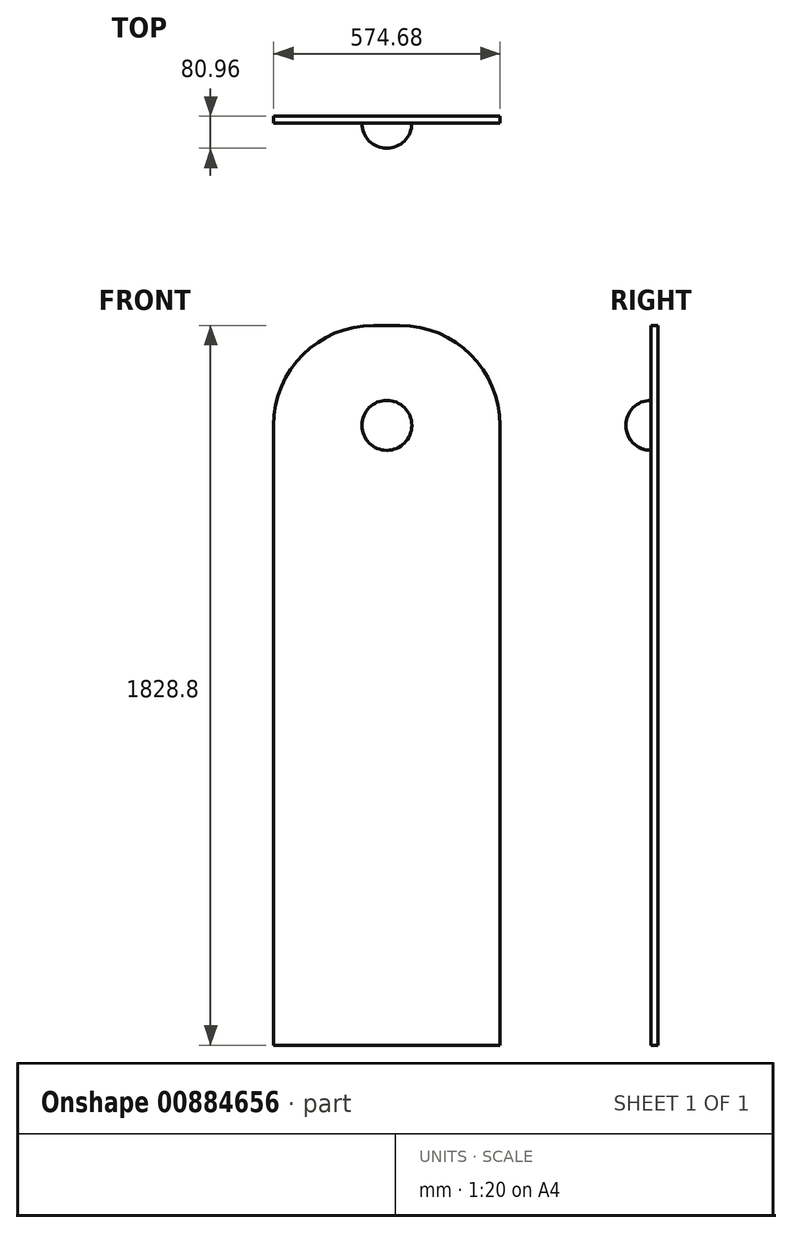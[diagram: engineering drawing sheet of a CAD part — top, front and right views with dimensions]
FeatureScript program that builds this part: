
annotation { "Feature Type Name" : "Feature", "Feature Type Description" : "" }
export const myFeature = defineFeature(function(context is Context, id is Id, definition is map)
    precondition{}
    {
        {
            var Q0;
            Q0=qCreatedBy(makeId("Front.planeOp"),FACE);
            var sketch = newSketch(context, id + "F0", { "sketchPlane" : qUnion([Q0])});
            skLineSegment(sketch, "E0.bottom", {"start": v(-1321.49, 910.36) * mm, "end": v(-746.81, 910.36) * mm});
            skLineSegment(sketch, "E0.top", {"start": v(-1321.49, -918.44) * mm, "end": v(-746.81, -918.44) * mm});
            skLineSegment(sketch, "E0.left", {"start": v(-1321.49, 910.36) * mm, "end": v(-1321.49, -918.44) * mm});
            skLineSegment(sketch, "E0.right", {"start": v(-746.81, 910.36) * mm, "end": v(-746.81, -918.44) * mm});
            skSolve(sketch);
        }
        {
            var Q0;
            Q0=makeQuery(id+"F0.imprint","IMPRINT",FACE,{"disambiguationData":[TD([[makeQuery(id+"F0.imprint","IMPRINT",EDGE,{"derivedFrom":sQuery(id+"F0.wireOp",EDGE,"E0.bottom")}),-1.0]])]});
            extrude(context, id + "F1", {"entities" : qUnion([Q0]), "depth" : 17.46 * mm, "offsetDistance" : 25.4 * mm});
        }
        {
            var Q0;
            Q0=makeQuery(id+"F1.opExtrude","SWEPT_EDGE",EDGE,{"disambiguationData":[OSD([sQuery(id+"F0.wireOp",EDGE,"E0.bottom"),sQuery(id+"F0.wireOp",EDGE,"E0.left")])]});
            fillet(context, id + "F2", {"entities" : qUnion([Q0]), "radius" : 254 * mm, "tangentPropagation" : true, "allowEdgeOverflow" : false});
        }
        {
            var Q0;
            Q0=makeQuery(id+"F1.opExtrude","SWEPT_EDGE",EDGE,{"disambiguationData":[OSD([sQuery(id+"F0.wireOp",EDGE,"E0.bottom"),sQuery(id+"F0.wireOp",EDGE,"E0.right")])]});
            fillet(context, id + "F3", {"entities" : qUnion([Q0]), "radius" : 254 * mm, "tangentPropagation" : true, "allowEdgeOverflow" : false});
        }
        {
            var Q0;
            Q0=makeQuery(id+"F1.opExtrude","CAP_FACE",FACE,{"disambiguationData":[OSD([sQuery(id+"F0.wireOp",EDGE,"E0.bottom"),sQuery(id+"F0.wireOp",EDGE,"E0.top"),sQuery(id+"F0.wireOp",EDGE,"E0.left"),sQuery(id+"F0.wireOp",EDGE,"E0.right")])],"isStart":false});
            var sketch = newSketch(context, id + "F4", { "sketchPlane" : qUnion([Q0])});
            skCircle(sketch, "E1", {"center": v(-1034.15, 656.36) * mm, "radius": 63.5 * mm});
            skSolve(sketch);
        }
        {
            var Q0;
            Q0=makeQuery(id+"F4.imprint","IMPRINT",FACE,{"disambiguationData":[TD([[makeQuery(id+"F4.imprint","IMPRINT",EDGE,{"derivedFrom":sQuery(id+"F4.wireOp",EDGE,"E1")}),1.0]])]});
            extrude(context, id + "F5", {"entities" : qUnion([Q0]), "operationType" : NewBodyOperationType.ADD, "depth" : 63.5 * mm, "offsetDistance" : 25.4 * mm});
        }
        {
            var Q0;
            Q0=makeQuery(id+"F5.opExtrude","CAP_EDGE",EDGE,{"disambiguationData":[OSD([sQuery(id+"F4.wireOp",EDGE,"E1")])],"isStart":false});
            fillet(context, id + "F6", {"entities" : qUnion([Q0]), "radius" : 63.5 * mm, "tangentPropagation" : true, "allowEdgeOverflow" : false});
        }
    });
